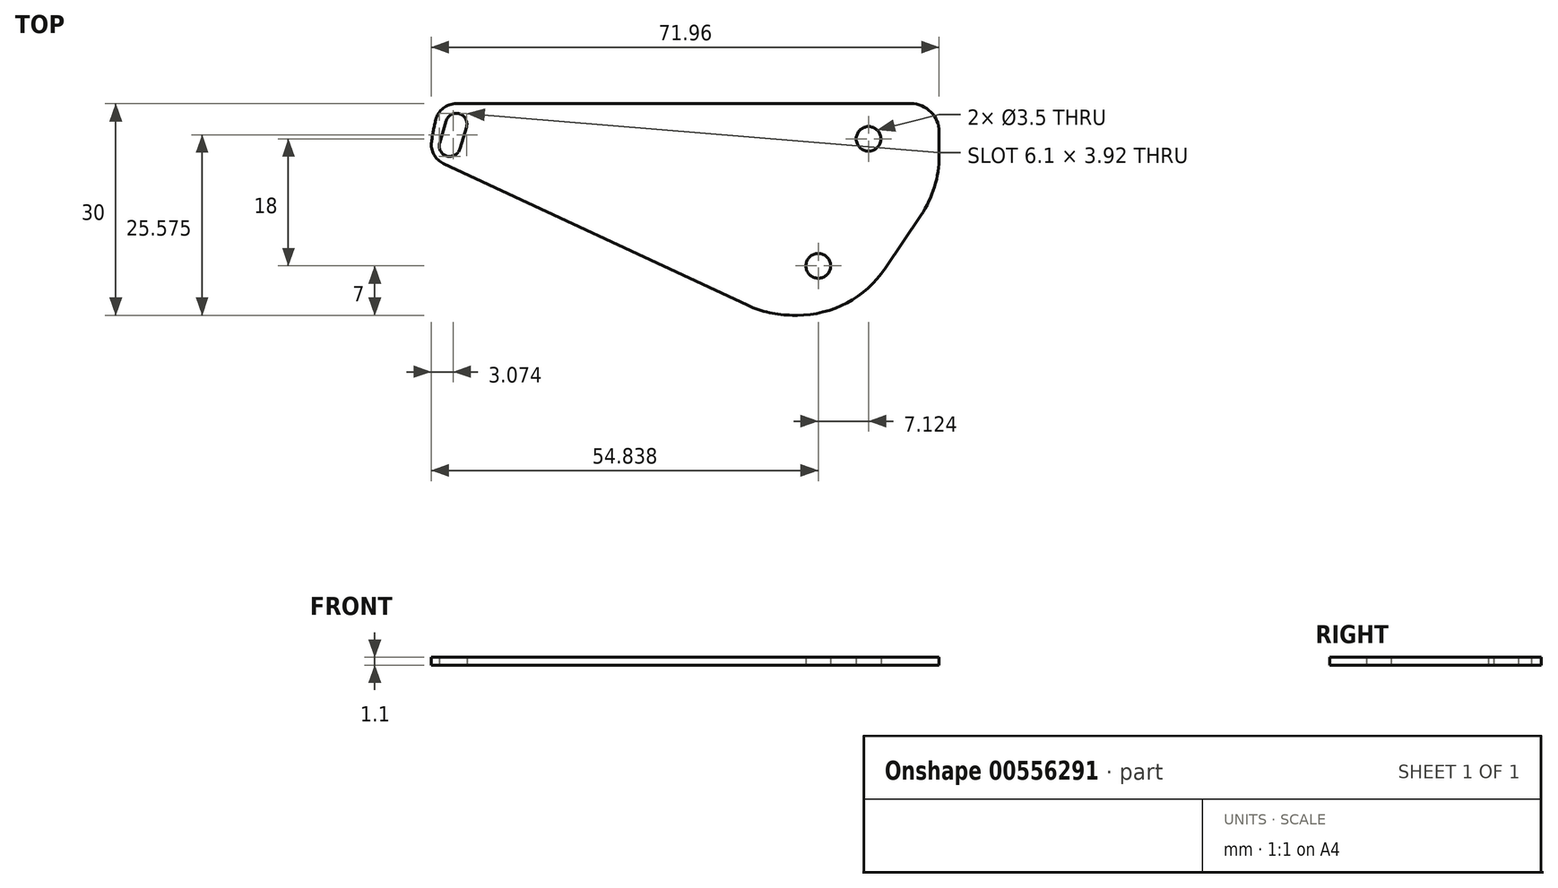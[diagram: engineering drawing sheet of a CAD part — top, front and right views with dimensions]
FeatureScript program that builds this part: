
annotation { "Feature Type Name" : "Feature", "Feature Type Description" : "" }
export const myFeature = defineFeature(function(context is Context, id is Id, definition is map)
    precondition{}
    {
        {
            var Q0;
            Q0=qCreatedBy(makeId("Top.planeOp"),FACE);
            var sketch = newSketch(context, id + "F0", { "sketchPlane" : qUnion([Q0])});
            skLineSegment(sketch, "E0", {"start": v(-22.68, 0) * mm, "end": v(22.32, 0) * mm});
            skLineSegment(sketch, "E1", {"start": v(22.32, 0) * mm, "end": v(74.88, 22.31) * mm});
            skLineSegment(sketch, "E2", {"start": v(-70.72, 22.4) * mm, "end": v(-22.68, 0) * mm});
            skLineSegment(sketch, "E3", {"start": v(91.1, 25) * mm, "end": v(-108.12, 25) * mm, "construction": true});
            skArc(sketch, "E4", {"start": v(-65.62, 25) * mm, "mid": v(-69.6, 25.3) * mm, "end": v(-65.7, 24.42) * mm, "construction": true});
            skCircle(sketch, "E5", {"center": v(-8.56, 25) * mm, "radius": 1.75 * mm});
            skCircle(sketch, "E6", {"center": v(69.44, 25) * mm, "radius": 1.75 * mm});
            skPoint(sketch, "E7", {"position": v(-70.56, 24.4) * mm});
            skLineSegment(sketch, "E8", {"start": v(74.88, 30) * mm, "end": v(-70.12, 30) * mm});
            skLineSegment(sketch, "E9", {"start": v(-70.12, 30) * mm, "end": v(-70.72, 22.4) * mm});
            skCircle(sketch, "E10", {"center": v(-15.68, 7) * mm, "radius": 1.75 * mm});
            skCircle(sketch, "E11", {"center": v(22.32, 15) * mm, "radius": 7.5 * mm});
            skLineSegment(sketch, "E12", {"start": v(74.88, 30) * mm, "end": v(74.88, 22.31) * mm});
            skLineSegment(sketch, "E13", {"start": v(22.32, 15) * mm, "end": v(22.32, 34.33) * mm, "construction": true});
            skCircle(sketch, "E14", {"center": v(18.1, 24.06) * mm, "radius": 1.5 * mm});
            skLineSegment(sketch, "E15", {"start": v(22.32, 15) * mm, "end": v(18.1, 24.06) * mm, "construction": true});
            skCircle(sketch, "E16.1.0", {"center": v(16.58, 6.8) * mm, "radius": 1.5 * mm});
            skCircle(sketch, "E16.2.0", {"center": v(32.28, 14.13) * mm, "radius": 1.5 * mm});
            skLineSegment(sketch, "E17", {"start": v(1.44, 18) * mm, "end": v(1.44, 30) * mm});
            skLineSegment(sketch, "E18", {"start": v(1.44, 18) * mm, "end": v(-10.68, 0) * mm});
            skLineSegment(sketch, "E19", {"start": v(-66.97, 27.15) * mm, "end": v(-67.62, 25) * mm, "construction": true});
            skArc(sketch, "E20", {"start": v(-68.9, 26.54) * mm, "mid": v(-67.55, 25.22) * mm, "end": v(-65.7, 25.59) * mm, "construction": true});
            skLineSegment(sketch, "E21", {"start": v(-66.97, 27.15) * mm, "end": v(-67.91, 24.02) * mm});
            skLineSegment(sketch, "E22", {"start": v(-67.62, 25) * mm, "end": v(-64.59, 24.09) * mm, "construction": true});
            skArc(sketch, "E23.MirrorC", {"start": v(-65.83, 25) * mm, "mid": v(-68.77, 21.88) * mm, "end": v(-68.73, 26.17) * mm, "construction": true});
            skLineSegment(sketch, "E24", {"start": v(-66.98, 27.13) * mm, "end": v(-67.91, 24.02) * mm});
            skArc(sketch, "E25.0.startCap", {"start": v(-68.42, 27.56) * mm, "mid": v(-66.55, 28.57) * mm, "end": v(-65.54, 26.7) * mm});
            skArc(sketch, "E25.0.endCap", {"start": v(-66.48, 23.59) * mm, "mid": v(-68.34, 22.58) * mm, "end": v(-69.35, 24.45) * mm});
            skLineSegment(sketch, "E25.0.left", {"start": v(-65.54, 26.7) * mm, "end": v(-66.48, 23.59) * mm});
            skLineSegment(sketch, "E25.0.right", {"start": v(-68.42, 27.56) * mm, "end": v(-69.35, 24.45) * mm});
            skPoint(sketch, "E26", {"position": v(-67.45, 25.57) * mm});
            skLineSegment(sketch, "E27", {"start": v(-71.46, 22.62) * mm, "end": v(-69.25, 30) * mm});
            skSolve(sketch);
        }
        {
            var Q0;
            {var subQ2=sQuery(id+"F0.wireOp",EDGE,"E2");Q0=makeQuery(id+"F0.imprint","IMPRINT",FACE,{"disambiguationData":[TD([[makeQuery(id+"F0.imprint","IMPRINT",EDGE,{"derivedFrom":subQ2}),1.0]])]});}
            extrude(context, id + "F1", {"entities" : qUnion([Q0]), "depth" : 1.1 * mm, "offsetDistance" : 25 * mm});
        }
        {
            var Q0;
            Q0=makeQuery(id+"F1.opExtrude","SWEPT_EDGE",EDGE,{"disambiguationData":[OSD([sQuery(id+"F0.wireOp",EDGE,"E8"),sQuery(id+"F0.wireOp",EDGE,"E17")])]});
            fillet(context, id + "F2", {"entities" : qUnion([Q0]), "radius" : 4 * mm, "tangentPropagation" : true, "allowEdgeOverflow" : false});
        }
        {
            var Q0;
            Q0=makeQuery(id+"F1.opExtrude","SWEPT_EDGE",EDGE,{"disambiguationData":[OSD([sQuery(id+"F0.wireOp",EDGE,"E9"),sQuery(id+"F0.wireOp",EDGE,"E27")])]});
            fillet(context, id + "F3", {"entities" : qUnion([Q0]), "radius" : 30 * mm, "tangentPropagation" : true, "allowEdgeOverflow" : false});
        }
        {
            var Q0;
            Q0=makeQuery(id+"F1.opExtrude","SWEPT_EDGE",EDGE,{"disambiguationData":[OSD([sQuery(id+"F0.wireOp",EDGE,"E0"),sQuery(id+"F0.wireOp",EDGE,"E2")])]});
            var Q1;
            Q1=makeQuery(id+"F1.opExtrude","SWEPT_EDGE",EDGE,{"disambiguationData":[OSD([sQuery(id+"F0.wireOp",EDGE,"E0"),sQuery(id+"F0.wireOp",EDGE,"E1")])]});
            var Q2;
            Q2=makeQuery(id+"F1.opExtrude","SWEPT_EDGE",EDGE,{"disambiguationData":[OSD([sQuery(id+"F0.wireOp",EDGE,"E17"),sQuery(id+"F0.wireOp",EDGE,"E18")])]});
            fillet(context, id + "F4", {"entities" : qUnion([Q0, Q1, Q2]), "radius" : 15 * mm, "tangentPropagation" : true, "allowEdgeOverflow" : false});
        }
        {
            var Q0;
            Q0=makeQuery(id+"F1.opExtrude","SWEPT_EDGE",EDGE,{"disambiguationData":[OSD([sQuery(id+"F0.wireOp",EDGE,"E8"),sQuery(id+"F0.wireOp",EDGE,"E27")])]});
            var Q1;
            Q1=makeQuery(id+"F1.opExtrude","SWEPT_EDGE",EDGE,{"disambiguationData":[OSD([sQuery(id+"F0.wireOp",EDGE,"E2"),sQuery(id+"F0.wireOp",EDGE,"E9")])]});
            fillet(context, id + "F5", {"entities" : qUnion([Q0, Q1]), "radius" : 3 * mm, "tangentPropagation" : true, "allowEdgeOverflow" : false});
        }
    });
